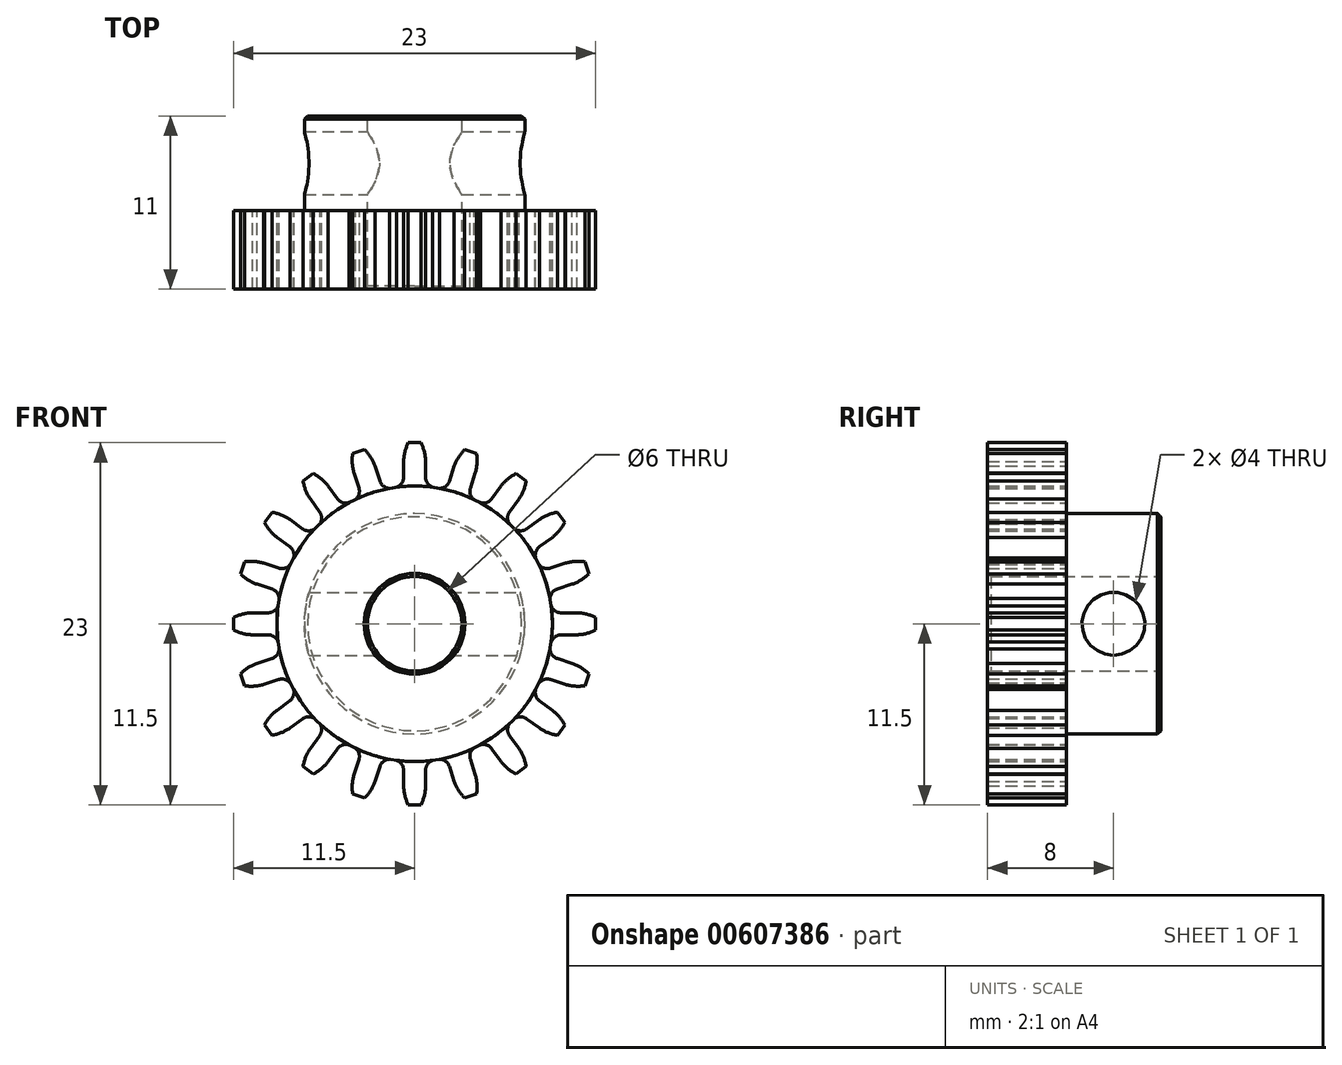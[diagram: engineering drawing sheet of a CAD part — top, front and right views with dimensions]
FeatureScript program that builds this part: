
annotation { "Feature Type Name" : "Feature", "Feature Type Description" : "" }
export const myFeature = defineFeature(function(context is Context, id is Id, definition is map)
    precondition{}
    {
        {
            var Q0;
            Q0=qCreatedBy(makeId("Front.planeOp"),FACE);
            var sketch = newSketch(context, id + "F0", { "sketchPlane" : qUnion([Q0])});
            skCircle(sketch, "E0", {"center": v(0, 0) * mm, "radius": 8.75 * mm, "construction": true});
            skCircle(sketch, "E1", {"center": v(0, 0) * mm, "radius": 11.5 * mm, "construction": true});
            skLineSegment(sketch, "E2", {"start": v(0, 11.5) * mm, "end": v(0.4, 11.5) * mm});
            skLineSegment(sketch, "E3", {"start": v(0, 11.5) * mm, "end": v(0, 8.75) * mm, "construction": true});
            skLineSegment(sketch, "E4", {"start": v(0, 10.3) * mm, "end": v(0.7, 10.3) * mm, "construction": true});
            skArc(sketch, "E5", {"start": v(0.7, 10.3) * mm, "mid": v(0.62, 10.92) * mm, "end": v(0.4, 11.5) * mm});
            skLineSegment(sketch, "E6", {"start": v(0.7, 10.3) * mm, "end": v(0.7, 9.3) * mm});
            skArc(sketch, "E7", {"start": v(0.7, 9.3) * mm, "mid": v(0.9, 8.82) * mm, "end": v(1.4, 8.64) * mm});
            skArc(sketch, "E8.MirrorCS", {"start": v(-0.7, 9.3) * mm, "mid": v(-0.9, 8.82) * mm, "end": v(-1.4, 8.64) * mm});
            skLineSegment(sketch, "E9.MirrorCS", {"start": v(0, 11.5) * mm, "end": v(-0.4, 11.5) * mm});
            skLineSegment(sketch, "E10.MirrorCS", {"start": v(-0.7, 10.3) * mm, "end": v(-0.7, 9.3) * mm});
            skArc(sketch, "E11.MirrorCS", {"start": v(-0.7, 10.3) * mm, "mid": v(-0.62, 10.92) * mm, "end": v(-0.4, 11.5) * mm});
            skArc(sketch, "E12", {"start": v(1.4, 8.64) * mm, "mid": v(0, 8.75) * mm, "end": v(-1.4, 8.64) * mm});
            skSolve(sketch);
        }
        {
            var Q0;
            Q0=makeQuery(id+"F0.imprint","IMPRINT",FACE,{"disambiguationData":[TD([[makeQuery(id+"F0.imprint","IMPRINT",EDGE,{"derivedFrom":sQuery(id+"F0.wireOp",EDGE,"E2")}),-1.0]])]});
            extrude(context, id + "F1", {"entities" : qUnion([Q0]), "depth" : 5 * mm, "offsetDistance" : 25 * mm});
        }
        {
            var Q0;
            Q0=qCreatedBy(makeId("Front.planeOp"),FACE);
            var sketch = newSketch(context, id + "F2", { "sketchPlane" : qUnion([Q0])});
            skCircle(sketch, "E13", {"center": v(0, 0) * mm, "radius": 8.75 * mm});
            skSolve(sketch);
        }
        {
            var Q0;
            Q0=qCreatedBy(makeId("Top.planeOp"),FACE);
            var sketch = newSketch(context, id + "F3", { "sketchPlane" : qUnion([Q0])});
            skLineSegment(sketch, "E14", {"start": v(0, 0) * mm, "end": v(0, -10.99) * mm, "construction": true});
            skSolve(sketch);
        }
        {
            var Q0;
            Q0=makeQuery(id+"F1.opExtrude","SWEPT_BODY",BODY,{"disambiguationData":[OSD([sQuery(id+"F0.wireOp",EDGE,"E2"),sQuery(id+"F0.wireOp",EDGE,"E5"),sQuery(id+"F0.wireOp",EDGE,"E6"),sQuery(id+"F0.wireOp",EDGE,"E7"),sQuery(id+"F0.wireOp",EDGE,"E8.MirrorCS"),sQuery(id+"F0.wireOp",EDGE,"E9.MirrorCS"),sQuery(id+"F0.wireOp",EDGE,"E10.MirrorCS"),sQuery(id+"F0.wireOp",EDGE,"E11.MirrorCS"),sQuery(id+"F0.wireOp",EDGE,"E12")])]});
            var Q1;
            Q1=sQuery(id+"F3.wireOp",EDGE,"E14");
            circularPattern(context, id + "F4", {"entities" : qUnion([Q0]), "axis" : qUnion([Q1]), "angle" : 6.28 * radian, "instanceCount" : 20, "equalSpace" : true, "isCentered" : true});
        }
        {
            var Q0;
            Q0=makeQuery(id+"F2.imprint","IMPRINT",FACE,{"disambiguationData":[TD([[makeQuery(id+"F2.imprint","IMPRINT",EDGE,{"derivedFrom":sQuery(id+"F2.wireOp",EDGE,"E13")}),1.0]])]});
            extrude(context, id + "F5", {"entities" : qUnion([Q0]), "depth" : 5 * mm, "offsetDistance" : 25 * mm});
        }
        {
            var Q0;
            Q0=makeQuery(id+"F5.opExtrude","CAP_FACE",FACE,{"disambiguationData":[OSD([sQuery(id+"F2.wireOp",EDGE,"E13")])],"isStart":true});
            var sketch = newSketch(context, id + "F6", { "sketchPlane" : qUnion([Q0])});
            skCircle(sketch, "E15", {"center": v(0, 0) * mm, "radius": 7 * mm});
            skSolve(sketch);
        }
        {
            var Q0;
            Q0 = qSketchRegion(id + "F6", true);
            extrude(context, id + "F7", {"entities" : qUnion([Q0]), "operationType" : NewBodyOperationType.ADD, "depth" : 6 * mm, "offsetDistance" : 25 * mm});
        }
        {
            var Q0;
            Q0=makeQuery(id+"F7.opExtrude","CAP_FACE",FACE,{"disambiguationData":[OSD([sQuery(id+"F6.wireOp",EDGE,"E15")])],"isStart":false});
            var sketch = newSketch(context, id + "F8", { "sketchPlane" : qUnion([Q0])});
            skCircle(sketch, "E16", {"center": v(0, 0) * mm, "radius": 3 * mm});
            skSolve(sketch);
        }
        {
            var Q0;
            Q0=makeQuery(id+"F8.imprint","IMPRINT",FACE,{"disambiguationData":[TD([[makeQuery(id+"F8.imprint","IMPRINT",EDGE,{"derivedFrom":sQuery(id+"F8.wireOp",EDGE,"E16")}),1.0]])]});
            var Q1;
            Q1=sQuery(id+"F8.wireOp",EDGE,"E16");
            extrude(context, id + "F9", {"entities" : qUnion([Q0]), "operationType" : NewBodyOperationType.REMOVE, "surfaceEntities" : qUnion([Q1]), "oppositeDirection" : true, "depth" : 25 * mm, "offsetDistance" : 25 * mm});
        }
        {
            var Q0;
            Q0=makeQuery(id+"F9.boolean.opBoolean","INTERSECT",EDGE,{"derivedFrom":[makeQuery(id+"F5.opExtrude","CAP_FACE",FACE,{"disambiguationData":[OSD([sQuery(id+"F2.wireOp",EDGE,"E13")])],"isStart":false}),makeQuery(id+"F9.opExtrude","SWEPT_FACE",FACE,{"disambiguationData":[OSD([sQuery(id+"F8.wireOp",EDGE,"E16")])]})]});
            var Q1;
            Q1=makeQuery(id+"F9.boolean.opBoolean","COPY",EDGE,{"derivedFrom":makeQuery(id+"F9.opExtrude","CAP_EDGE",EDGE,{"disambiguationData":[OSD([sQuery(id+"F8.wireOp",EDGE,"E16")])],"isStart":true})});
            var Q2;
            Q2=makeQuery(id+"F7.opExtrude","CAP_EDGE",EDGE,{"disambiguationData":[OSD([sQuery(id+"F6.wireOp",EDGE,"E15")])],"isStart":false});
            chamfer(context, id + "F10", {"entities" : qUnion([Q0, Q1, Q2]), "width" : 0.2 * mm, "tangentPropagation" : true});
        }
        {
            var Q0;
            Q0=qCreatedBy(makeId("Right.planeOp"),FACE);
            var sketch = newSketch(context, id + "F11", { "sketchPlane" : qUnion([Q0])});
            skLineSegment(sketch, "E17", {"start": v(0, 0) * mm, "end": v(6, 0) * mm, "construction": true});
            skCircle(sketch, "E18", {"center": v(3, 0) * mm, "radius": 2 * mm});
            skSolve(sketch);
        }
        {
            var Q0;
            Q0=makeQuery(id+"F11.imprint","IMPRINT",FACE,{"disambiguationData":[TD([[makeQuery(id+"F11.imprint","IMPRINT",EDGE,{"derivedFrom":sQuery(id+"F11.wireOp",EDGE,"E18")}),1.0]])]});
            var Q1;
            Q1=sQuery(id+"F11.wireOp",EDGE,"E18");
            extrude(context, id + "F12", {"entities" : qUnion([Q0]), "operationType" : NewBodyOperationType.REMOVE, "surfaceEntities" : qUnion([Q1]), "oppositeDirection" : true, "depth" : 25 * mm, "offsetDistance" : 25 * mm, "hasSecondDirection" : true, "secondDirectionOppositeDirection" : false, "secondDirectionDepth" : 25 * mm});
        }
    });
